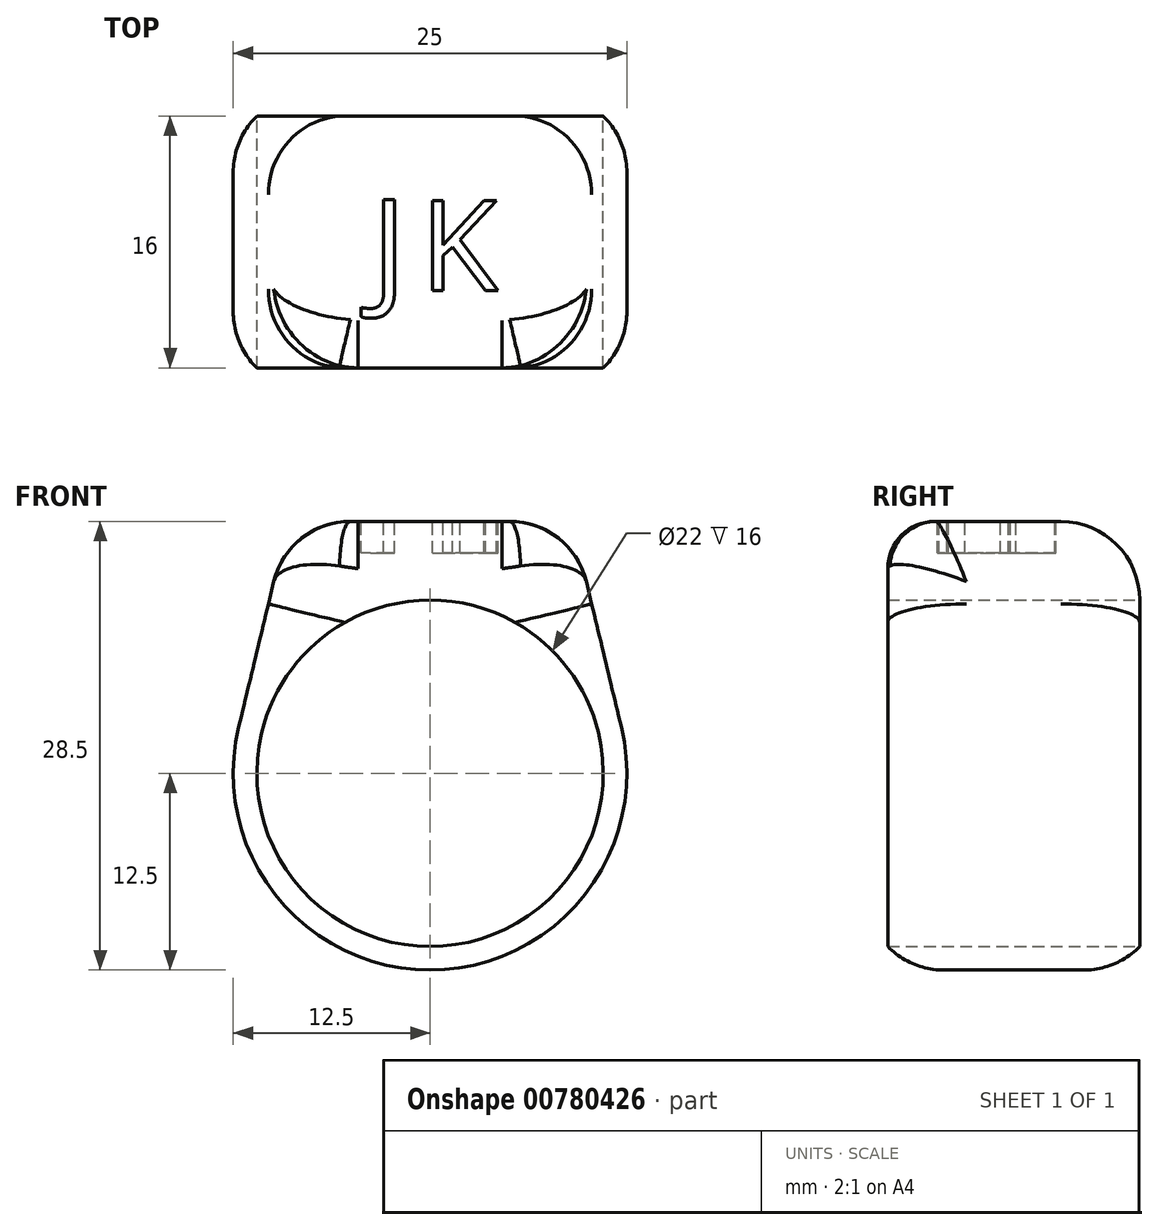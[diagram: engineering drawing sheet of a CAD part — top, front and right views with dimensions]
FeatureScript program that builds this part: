
annotation { "Feature Type Name" : "Feature", "Feature Type Description" : "" }
export const myFeature = defineFeature(function(context is Context, id is Id, definition is map)
    precondition{}
    {
        {
            var Q0;
            Q0=qCreatedBy(makeId("Front.planeOp"),FACE);
            var sketch = newSketch(context, id + "F0", { "sketchPlane" : qUnion([Q0])});
            skCircle(sketch, "E0", {"center": v(0, 0) * mm, "radius": 11 * mm});
            skArc(sketch, "E1", {"start": v(-3.5, 12) * mm, "mid": v(0, -12.5) * mm, "end": v(3.5, 12) * mm});
            skLineSegment(sketch, "E2", {"start": v(-3.5, 12) * mm, "end": v(3.5, 12) * mm});
            skPoint(sketch, "E3.orphan", {"position": v(12.9, 17) * mm});
            skPoint(sketch, "E4.end.orphan", {"position": v(12.9, 11) * mm});
            skSolve(sketch);
        }
        {
            var Q0;
            Q0 = qSketchRegion(id + "F0", true);
            extrude(context, id + "F1", {"entities" : qUnion([Q0]), "depth" : 16 * mm, "offsetDistance" : 25 * mm});
        }
        {
            var Q0;
            Q0=makeQuery(id+"F1.opExtrude","SWEPT_FACE",FACE,{"disambiguationData":[OSD([sQuery(id+"F0.wireOp",EDGE,"E2")])]});
            var sketch = newSketch(context, id + "F2", { "sketchPlane" : qUnion([Q0])});
            skLineSegment(sketch, "E5", {"start": v(-9, 0) * mm, "end": v(-9, -16) * mm});
            skLineSegment(sketch, "E6", {"start": v(-9, -16) * mm, "end": v(9, -16) * mm});
            skLineSegment(sketch, "E7", {"start": v(9, -16) * mm, "end": v(9, 0) * mm});
            skLineSegment(sketch, "E8", {"start": v(9, 0) * mm, "end": v(-9, 0) * mm});
            skSolve(sketch);
        }
        {
            var Q0;
            Q0 = qSketchRegion(id + "F2", true);
            extrude(context, id + "F3", {"entities" : qUnion([Q0]), "operationType" : NewBodyOperationType.ADD, "depth" : 4 * mm, "offsetDistance" : 25 * mm});
        }
        {
            var Q0;
            Q0=makeQuery(id+"F3.boolean.opBoolean","MERGE",FACE,{"derivedFrom":[makeQuery(id+"F1.opExtrude","CAP_FACE",FACE,{"disambiguationData":[OSD([sQuery(id+"F0.wireOp",EDGE,"E0"),sQuery(id+"F0.wireOp",EDGE,"E1"),sQuery(id+"F0.wireOp",EDGE,"E2")])],"isStart":false}),makeQuery(id+"F3.opExtrude","SWEPT_FACE",FACE,{"disambiguationData":[OSD([sQuery(id+"F2.wireOp",EDGE,"E6")])]})]});
            var sketch = newSketch(context, id + "F4", { "sketchPlane" : qUnion([Q0])});
            skLineSegment(sketch, "E9", {"start": v(-9, 12) * mm, "end": v(-9, 8.67) * mm});
            skLineSegment(sketch, "E10", {"start": v(9, 12) * mm, "end": v(9, 8.68) * mm});
            skSolve(sketch);
        }
        {
            var Q0;
            Q0 = qSketchRegion(id + "F4", true);
            var Q1;
            {var subQ0=sQuery(id+"F4.wireOp",EDGE,"E9");Q1=makeQuery(id+"F4.imprint","IMPRINT",FACE,{"disambiguationData":[TD([[makeQuery(id+"F4.imprint","IMPRINT",EDGE,{"derivedFrom":subQ0}),1.0]])]});}
            var Q2;
            {var subQ0=sQuery(id+"F4.wireOp",EDGE,"E10");Q2=makeQuery(id+"F4.imprint","IMPRINT",FACE,{"disambiguationData":[TD([[makeQuery(id+"F4.imprint","IMPRINT",EDGE,{"derivedFrom":subQ0}),-1.0]])]});}
            extrude(context, id + "F5", {"entities" : qUnion([Q0, Q1, Q2]), "operationType" : NewBodyOperationType.ADD, "oppositeDirection" : true, "depth" : 16 * mm, "offsetDistance" : 25 * mm});
        }
        {
            var Q0;
            {var subQ0=sQuery(id+"F2.wireOp",EDGE,"E6");var subQ1=sQuery(id+"F0.wireOp",EDGE,"E1");Q0=makeQuery(id+"F5.boolean.opBoolean","MERGE",FACE,{"derivedFrom":[makeQuery(id+"F3.boolean.opBoolean","MERGE",FACE,{"derivedFrom":[makeQuery(id+"F1.opExtrude","CAP_FACE",FACE,{"disambiguationData":[OSD([sQuery(id+"F0.wireOp",EDGE,"E0"),subQ1,sQuery(id+"F0.wireOp",EDGE,"E2")])],"isStart":false}),makeQuery(id+"F3.opExtrude","SWEPT_FACE",FACE,{"disambiguationData":[OSD([subQ0])]})]}),makeQuery(id+"F5.opExtrude","CAP_FACE",FACE,{"disambiguationData":[OSD([subQ1,subQ0,sQuery(id+"F4.wireOp",EDGE,"E9")])],"isStart":true}),makeQuery(id+"F5.opExtrude","CAP_FACE",FACE,{"disambiguationData":[OSD([subQ1,subQ0,sQuery(id+"F4.wireOp",EDGE,"E10")])],"isStart":true})]});}
            var sketch = newSketch(context, id + "F6", { "sketchPlane" : qUnion([Q0])});
            skLineSegment(sketch, "E11", {"start": v(-9, 16) * mm, "end": v(-12.15, 2.93) * mm});
            skLineSegment(sketch, "E12", {"start": v(9, 16) * mm, "end": v(12.15, 2.93) * mm});
            skSolve(sketch);
        }
        {
            var Q0;
            Q0 = qSketchRegion(id + "F6", true);
            var Q1;
            {var subQ0=sQuery(id+"F6.wireOp",EDGE,"E11");Q1=makeQuery(id+"F6.imprint","IMPRINT",FACE,{"disambiguationData":[TD([[makeQuery(id+"F6.imprint","IMPRINT",EDGE,{"derivedFrom":subQ0}),1.0]])]});}
            var Q2;
            {var subQ0=sQuery(id+"F6.wireOp",EDGE,"E12");Q2=makeQuery(id+"F6.imprint","IMPRINT",FACE,{"disambiguationData":[TD([[makeQuery(id+"F6.imprint","IMPRINT",EDGE,{"derivedFrom":subQ0}),-1.0]])]});}
            extrude(context, id + "F7", {"entities" : qUnion([Q0, Q1, Q2]), "operationType" : NewBodyOperationType.ADD, "oppositeDirection" : true, "depth" : 16 * mm, "offsetDistance" : 25 * mm});
        }
        {
            var Q0;
            Q0=makeQuery(id+"F3.opExtrude","CAP_EDGE",EDGE,{"disambiguationData":[OSD([sQuery(id+"F2.wireOp",EDGE,"E6")])],"isStart":false});
            fillet(context, id + "F8", {"entities" : qUnion([Q0]), "radius" : 3 * mm, "tangentPropagation" : true, "allowEdgeOverflow" : false});
        }
        {
            var Q0;
            {var subQ0=sQuery(id+"F2.wireOp",EDGE,"E7");Q0=makeQuery(id+"F7.boolean.opBoolean","MERGE",EDGE,{"derivedFrom":[makeQuery(id+"F3.opExtrude","CAP_EDGE",EDGE,{"disambiguationData":[OSD([subQ0])],"isStart":false}),makeQuery(id+"F7.opExtrude","SWEPT_EDGE",EDGE,{"disambiguationData":[OSD([sQuery(id+"F2.wireOp",EDGE,"E6"),subQ0,sQuery(id+"F4.wireOp",EDGE,"E10"),sQuery(id+"F6.wireOp",EDGE,"E12")])]})]});}
            var Q1;
            Q1=makeQuery(id+"F3.opExtrude","CAP_EDGE",EDGE,{"disambiguationData":[OSD([sQuery(id+"F2.wireOp",EDGE,"E8")])],"isStart":false});
            fillet(context, id + "F9", {"entities" : qUnion([Q0, Q1]), "radius" : 5 * mm, "tangentPropagation" : true, "allowEdgeOverflow" : false});
        }
        {
            var Q0;
            {var subQ0=sQuery(id+"F2.wireOp",EDGE,"E5");Q0=makeQuery(id+"F9.opFillet","BLEND_EDGE",EDGE,{"blendedFrom":[makeQuery(id+"F3.opExtrude","CAP_EDGE",EDGE,{"disambiguationData":[OSD([sQuery(id+"F2.wireOp",EDGE,"E8")])],"isStart":false}),makeQuery(id+"F7.boolean.opBoolean","MERGE",EDGE,{"derivedFrom":[makeQuery(id+"F3.opExtrude","CAP_EDGE",EDGE,{"disambiguationData":[OSD([subQ0])],"isStart":false}),makeQuery(id+"F7.opExtrude","SWEPT_EDGE",EDGE,{"disambiguationData":[OSD([subQ0,sQuery(id+"F2.wireOp",EDGE,"E6"),sQuery(id+"F4.wireOp",EDGE,"E9"),sQuery(id+"F6.wireOp",EDGE,"E11")])]})]})],"blendedInto":[]});}
            fillet(context, id + "F10", {"entities" : qUnion([Q0]), "radius" : 5 * mm, "tangentPropagation" : true, "allowEdgeOverflow" : false});
        }
        {
            var Q0;
            Q0=makeQuery(id+"F3.opExtrude","CAP_FACE",FACE,{"disambiguationData":[OSD([sQuery(id+"F2.wireOp",EDGE,"E5"),sQuery(id+"F2.wireOp",EDGE,"E6"),sQuery(id+"F2.wireOp",EDGE,"E7"),sQuery(id+"F2.wireOp",EDGE,"E8")])],"isStart":false});
            var sketch = newSketch(context, id + "F11", { "sketchPlane" : qUnion([Q0])});
            skText(sketch, "E13", { "text": "J", "fontName": "OpenSans-Regular.ttf"});
            skText(sketch, "E14", { "text": "K", "fontName": "OpenSans-Regular.ttf"});
            const initialGuessF11  = {"E13": [-0.00373, -0.01128, 1, 0, 0.00602], "E14": [-0.00062, -0.0111, 1, 0, 0.00578]};
            skSetInitialGuess(sketch, initialGuessF11);
            skSolve(sketch);
        }
        {
            var Q0;
            Q0 = qSketchRegion(id + "F11", true);
            extrude(context, id + "F12", {"entities" : qUnion([Q0]), "operationType" : NewBodyOperationType.REMOVE, "oppositeDirection" : true, "depth" : 2 * mm, "offsetDistance" : 25 * mm});
        }
    });
